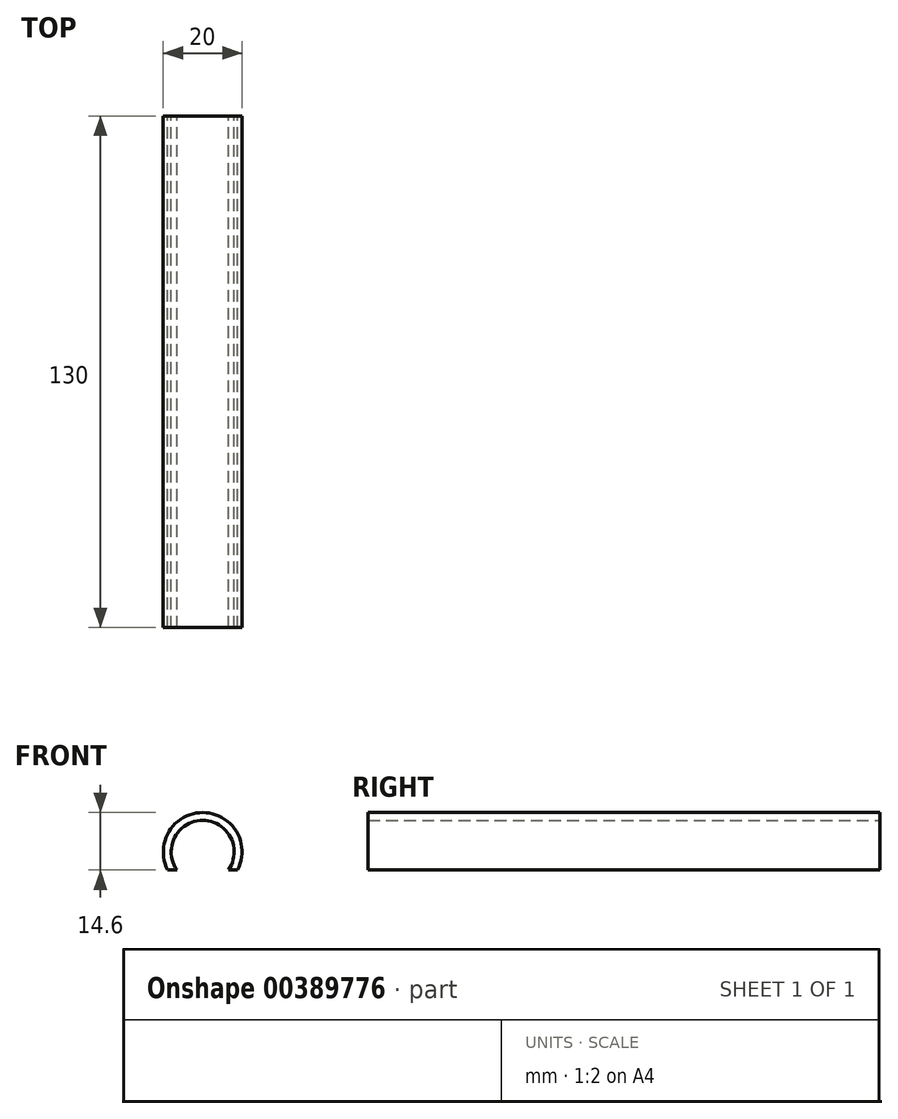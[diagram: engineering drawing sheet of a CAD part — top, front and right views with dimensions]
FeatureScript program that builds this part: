
annotation { "Feature Type Name" : "Feature", "Feature Type Description" : "" }
export const myFeature = defineFeature(function(context is Context, id is Id, definition is map)
    precondition{}
    {
        {
            var Q0;
            Q0=qCreatedBy(makeId("Front.planeOp"),FACE);
            var sketch = newSketch(context, id + "F0", { "sketchPlane" : qUnion([Q0])});
            skArc(sketch, "E0", {"start": v(8.88, -4.6) * mm, "mid": v(0, 10) * mm, "end": v(-8.88, -4.6) * mm});
            skArc(sketch, "E1", {"start": v(6.55, -4.6) * mm, "mid": v(0, 8) * mm, "end": v(-6.55, -4.6) * mm});
            skLineSegment(sketch, "E2", {"start": v(-8.88, -4.6) * mm, "end": v(-6.55, -4.6) * mm});
            skLineSegment(sketch, "E3.trimOffspring", {"start": v(6.55, -4.6) * mm, "end": v(8.88, -4.6) * mm});
            skSolve(sketch);
        }
        {
            var Q0;
            Q0 = qSketchRegion(id + "F0", true);
            extrude(context, id + "F1", {"entities" : qUnion([Q0]), "depth" : 130 * mm});
        }
    });
